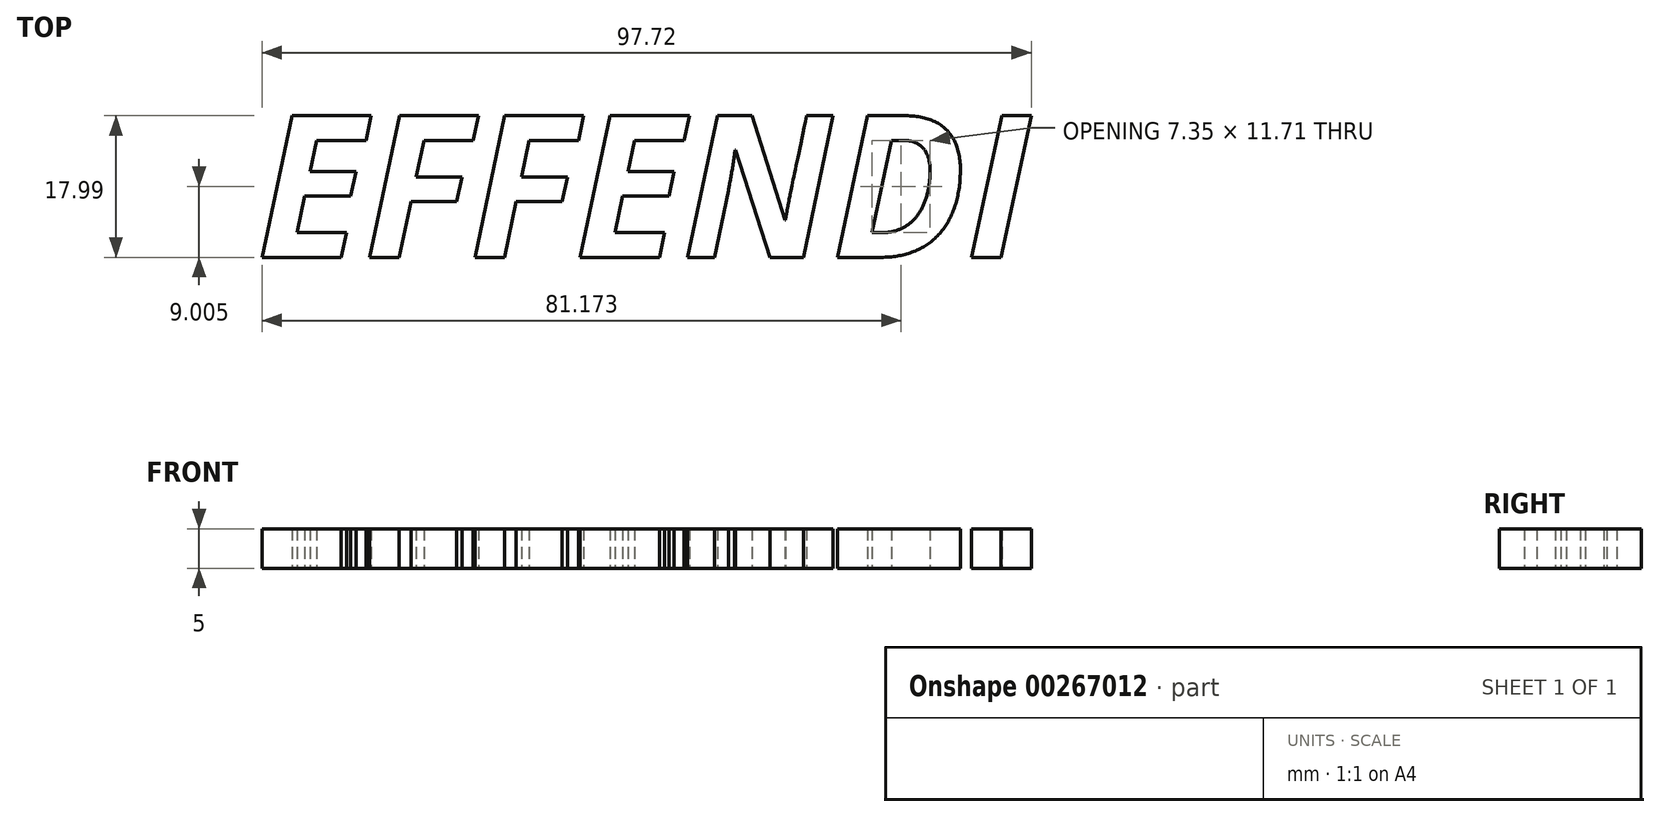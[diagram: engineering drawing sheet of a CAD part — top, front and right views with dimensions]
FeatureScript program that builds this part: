
annotation { "Feature Type Name" : "Feature", "Feature Type Description" : "" }
export const myFeature = defineFeature(function(context is Context, id is Id, definition is map)
    precondition{}
    {
        {
            var Q0;
            Q0=qCreatedBy(makeId("Top.planeOp"),FACE);
            var sketch = newSketch(context, id + "F0", { "sketchPlane" : qUnion([Q0])});
            skText(sketch, "E0", { "text": "EFFENDI", "fontName": "OpenSans-BoldItalic.ttf"});
            const initialGuessF0  = {"E0": [-0.0424, -0.00843, 1, 0, 0.01814]};
            skSetInitialGuess(sketch, initialGuessF0);
            skSolve(sketch);
        }
        {
            var Q0;
            Q0 = qSketchRegion(id + "F0", true);
            extrude(context, id + "F1", {"entities" : qUnion([Q0]), "depth" : 5 * mm});
        }
    });
